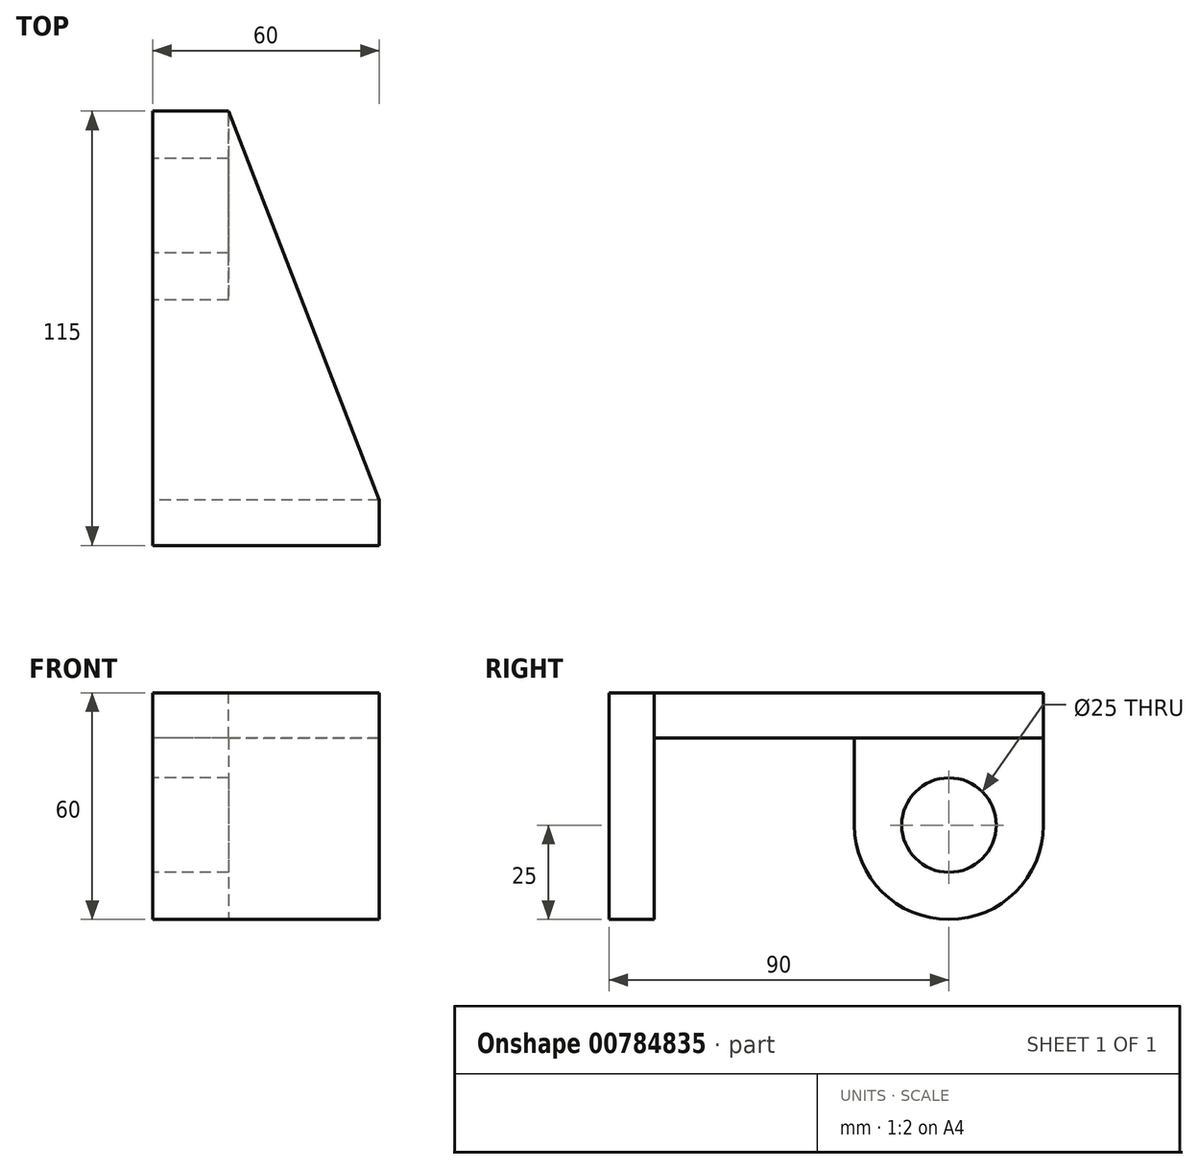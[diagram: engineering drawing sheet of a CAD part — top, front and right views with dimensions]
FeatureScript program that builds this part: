
annotation { "Feature Type Name" : "Feature", "Feature Type Description" : "" }
export const myFeature = defineFeature(function(context is Context, id is Id, definition is map)
    precondition{}
    {
        {
            var Q0;
            Q0=qCreatedBy(makeId("Front.planeOp"),FACE);
            var sketch = newSketch(context, id + "F0", { "sketchPlane" : qUnion([Q0])});
            skLineSegment(sketch, "E0.bottom", {"start": v(30, 30) * mm, "end": v(-30, 30) * mm});
            skLineSegment(sketch, "E0.top", {"start": v(30, -30) * mm, "end": v(-30, -30) * mm});
            skLineSegment(sketch, "E0.left", {"start": v(30, 30) * mm, "end": v(30, -30) * mm});
            skLineSegment(sketch, "E0.right", {"start": v(-30, 30) * mm, "end": v(-30, -30) * mm});
            skPoint(sketch, "E0.middle", {"position": v(0, 0) * mm});
            skSolve(sketch);
        }
        {
            var Q0;
            Q0=makeQuery(id+"F0.imprint","IMPRINT",FACE,{"disambiguationData":[TD([[makeQuery(id+"F0.imprint","IMPRINT",EDGE,{"derivedFrom":sQuery(id+"F0.wireOp",EDGE,"E0.bottom")}),1.0]])]});
            extrude(context, id + "F1", {"entities" : qUnion([Q0]), "depth" : 12 * mm, "offsetDistance" : 25 * mm});
        }
        {
            var Q0;
            Q0=makeQuery(id+"F1.opExtrude","SWEPT_FACE",FACE,{"disambiguationData":[OSD([sQuery(id+"F0.wireOp",EDGE,"E0.bottom")])]});
            var sketch = newSketch(context, id + "F2", { "sketchPlane" : qUnion([Q0])});
            skLineSegment(sketch, "E1", {"start": v(-30, 0) * mm, "end": v(-30, 103) * mm});
            skLineSegment(sketch, "E2", {"start": v(30, 0) * mm, "end": v(-30, 0) * mm});
            skLineSegment(sketch, "E3", {"start": v(-30, 103) * mm, "end": v(-10, 103) * mm});
            skLineSegment(sketch, "E4", {"start": v(-10, 103) * mm, "end": v(30, 0) * mm});
            skSolve(sketch);
        }
        {
            var Q0;
            Q0=makeQuery(id+"F2.imprint","IMPRINT",FACE,{"disambiguationData":[TD([[makeQuery(id+"F2.imprint","IMPRINT",EDGE,{"derivedFrom":sQuery(id+"F2.wireOp",EDGE,"E1")}),-1.0]])]});
            extrude(context, id + "F3", {"entities" : qUnion([Q0]), "operationType" : NewBodyOperationType.ADD, "oppositeDirection" : true, "depth" : 12 * mm, "offsetDistance" : 25 * mm});
        }
        {
            var Q0;
            Q0=makeQuery(id+"F3.boolean.opBoolean","MERGE",FACE,{"derivedFrom":[makeQuery(id+"F1.opExtrude","SWEPT_FACE",FACE,{"disambiguationData":[OSD([sQuery(id+"F0.wireOp",EDGE,"E0.right")])]}),makeQuery(id+"F3.opExtrude","SWEPT_FACE",FACE,{"disambiguationData":[OSD([sQuery(id+"F2.wireOp",EDGE,"E1")])]})]});
            var sketch = newSketch(context, id + "F4", { "sketchPlane" : qUnion([Q0])});
            skLineSegment(sketch, "E5.bottom", {"start": v(-103, 18) * mm, "end": v(-53, 18) * mm});
            skLineSegment(sketch, "E5.top", {"start": v(-103, -5) * mm, "end": v(-53, -5) * mm});
            skLineSegment(sketch, "E5.left", {"start": v(-103, 18) * mm, "end": v(-103, -5) * mm});
            skLineSegment(sketch, "E5.right", {"start": v(-53, 18) * mm, "end": v(-53, -5) * mm});
            skSolve(sketch);
        }
        {
            var Q0;
            Q0=makeQuery(id+"F4.imprint","IMPRINT",FACE,{"disambiguationData":[TD([[makeQuery(id+"F4.imprint","IMPRINT",EDGE,{"derivedFrom":sQuery(id+"F4.wireOp",EDGE,"E5.bottom")}),1.0]])]});
            extrude(context, id + "F5", {"entities" : qUnion([Q0]), "operationType" : NewBodyOperationType.ADD, "oppositeDirection" : true, "depth" : 20 * mm, "offsetDistance" : 25 * mm});
        }
        {
            var Q0;
            Q0=makeQuery(id+"F5.boolean.opBoolean","MERGE",FACE,{"derivedFrom":[makeQuery(id+"F3.boolean.opBoolean","MERGE",FACE,{"derivedFrom":[makeQuery(id+"F1.opExtrude","SWEPT_FACE",FACE,{"disambiguationData":[OSD([sQuery(id+"F0.wireOp",EDGE,"E0.right")])]}),makeQuery(id+"F3.opExtrude","SWEPT_FACE",FACE,{"disambiguationData":[OSD([sQuery(id+"F2.wireOp",EDGE,"E1")])]})]}),makeQuery(id+"F5.opExtrude","CAP_FACE",FACE,{"disambiguationData":[OSD([sQuery(id+"F4.wireOp",EDGE,"E5.bottom"),sQuery(id+"F4.wireOp",EDGE,"E5.top"),sQuery(id+"F4.wireOp",EDGE,"E5.left"),sQuery(id+"F4.wireOp",EDGE,"E5.right")])],"isStart":true})]});
            var sketch = newSketch(context, id + "F6", { "sketchPlane" : qUnion([Q0])});
            skArc(sketch, "E6", {"start": v(-103, -5) * mm, "mid": v(-78, -30) * mm, "end": v(-53, -5) * mm});
            skSolve(sketch);
        }
        {
            var Q0;
            Q0=makeQuery(id+"F6.imprint","IMPRINT",FACE,{"disambiguationData":[TD([[makeQuery(id+"F6.imprint","IMPRINT",EDGE,{"derivedFrom":sQuery(id+"F6.wireOp",EDGE,"E6")}),1.0]])]});
            extrude(context, id + "F7", {"entities" : qUnion([Q0]), "operationType" : NewBodyOperationType.ADD, "oppositeDirection" : true, "depth" : 20 * mm, "offsetDistance" : 25 * mm});
        }
        {
            var Q0;
            {var subQ0=sQuery(id+"F4.wireOp",EDGE,"E5.top");Q0=makeQuery(id+"F7.boolean.opBoolean","MERGE",FACE,{"derivedFrom":[makeQuery(id+"F5.boolean.opBoolean","MERGE",FACE,{"derivedFrom":[makeQuery(id+"F3.boolean.opBoolean","MERGE",FACE,{"derivedFrom":[makeQuery(id+"F1.opExtrude","SWEPT_FACE",FACE,{"disambiguationData":[OSD([sQuery(id+"F0.wireOp",EDGE,"E0.right")])]}),makeQuery(id+"F3.opExtrude","SWEPT_FACE",FACE,{"disambiguationData":[OSD([sQuery(id+"F2.wireOp",EDGE,"E1")])]})]}),makeQuery(id+"F5.opExtrude","CAP_FACE",FACE,{"disambiguationData":[OSD([sQuery(id+"F4.wireOp",EDGE,"E5.bottom"),subQ0,sQuery(id+"F4.wireOp",EDGE,"E5.left"),sQuery(id+"F4.wireOp",EDGE,"E5.right")])],"isStart":true})]}),makeQuery(id+"F7.opExtrude","CAP_FACE",FACE,{"disambiguationData":[OSD([subQ0,sQuery(id+"F6.wireOp",EDGE,"E6")])],"isStart":true})]});}
            var sketch = newSketch(context, id + "F8", { "sketchPlane" : qUnion([Q0])});
            skCircle(sketch, "E7", {"center": v(-78, -5) * mm, "radius": 12.5 * mm});
            skSolve(sketch);
        }
        {
            var Q0;
            Q0=makeQuery(id+"F8.imprint","IMPRINT",FACE,{"disambiguationData":[TD([[makeQuery(id+"F8.imprint","IMPRINT",EDGE,{"derivedFrom":sQuery(id+"F8.wireOp",EDGE,"E7")}),1.0]])]});
            extrude(context, id + "F9", {"entities" : qUnion([Q0]), "operationType" : NewBodyOperationType.REMOVE, "oppositeDirection" : true, "depth" : 20 * mm, "offsetDistance" : 25 * mm});
        }
    });
